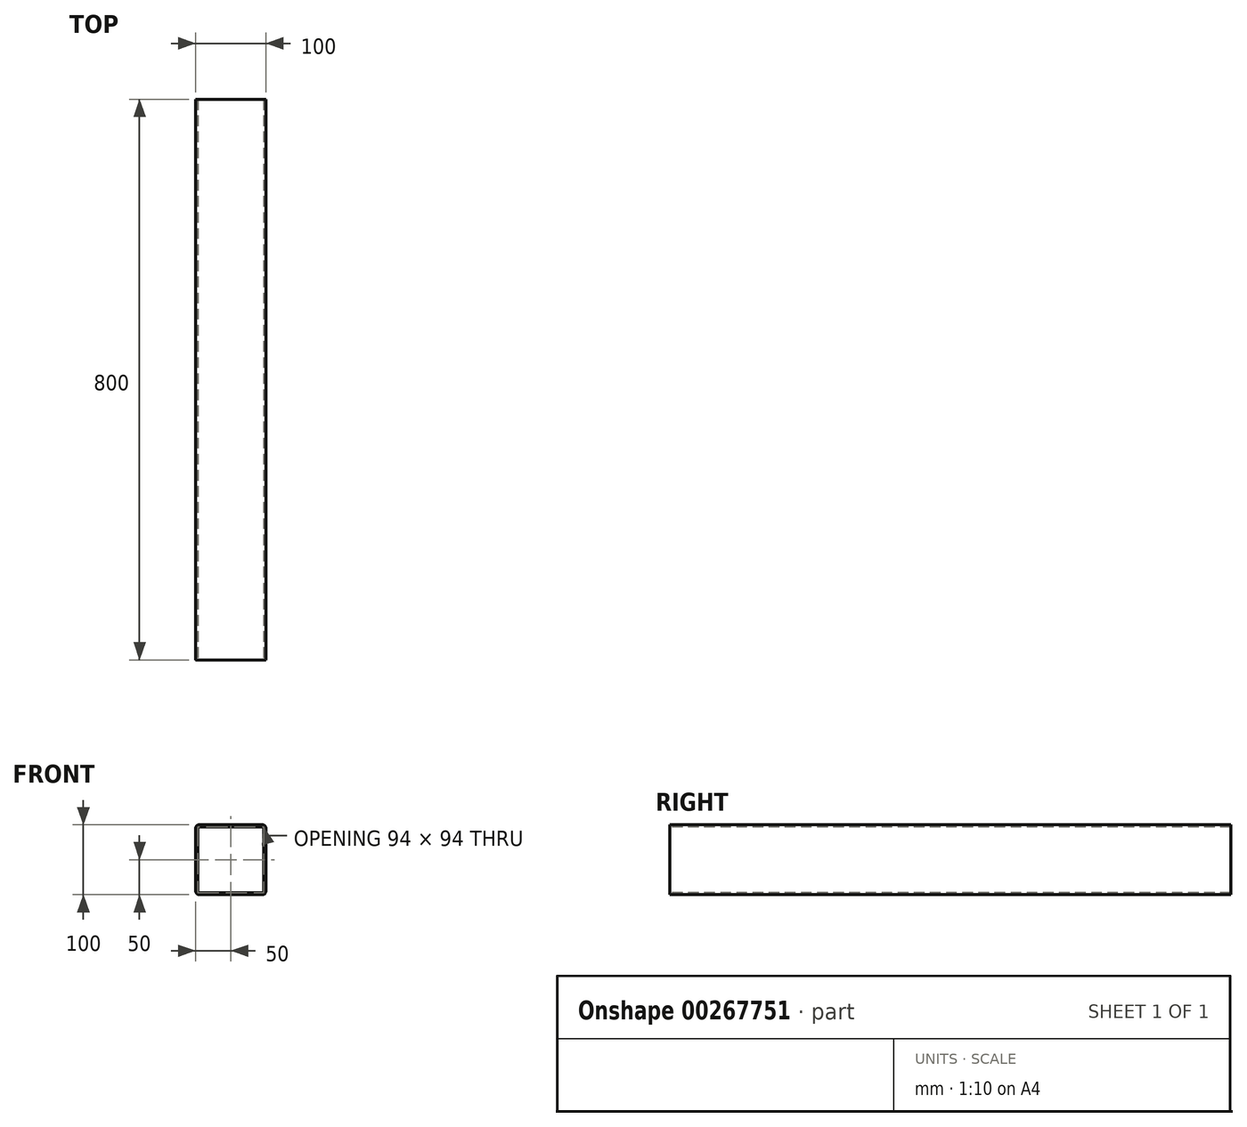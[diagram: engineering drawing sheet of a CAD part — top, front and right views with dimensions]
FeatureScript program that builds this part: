
annotation { "Feature Type Name" : "Feature", "Feature Type Description" : "" }
export const myFeature = defineFeature(function(context is Context, id is Id, definition is map)
    precondition{}
    {
        {
            var Q0;
            Q0=qCreatedBy(makeId("Front.planeOp"),FACE);
            var sketch = newSketch(context, id + "F0", { "sketchPlane" : qUnion([Q0])});
            skLineSegment(sketch, "E0.bottom", {"start": v(45, 50) * mm, "end": v(-45, 50) * mm});
            skLineSegment(sketch, "E0.top", {"start": v(45, -50) * mm, "end": v(-45, -50) * mm});
            skLineSegment(sketch, "E0.left", {"start": v(50, 45) * mm, "end": v(50, -45) * mm});
            skLineSegment(sketch, "E0.right", {"start": v(-50, 45) * mm, "end": v(-50, -45) * mm});
            skPoint(sketch, "E0.middle", {"position": v(0, 0) * mm});
            skPoint(sketch, "E1.visualSharp", {"position": v(-50, 50) * mm});
            skArc(sketch, "E1.filletArc", {"start": v(-45, 50) * mm, "mid": v(-48.54, 48.54) * mm, "end": v(-50, 45) * mm});
            skPoint(sketch, "E2.visualSharp", {"position": v(50, 50) * mm});
            skArc(sketch, "E2.filletArc", {"start": v(50, 45) * mm, "mid": v(48.54, 48.54) * mm, "end": v(45, 50) * mm});
            skPoint(sketch, "E3.visualSharp", {"position": v(50, -50) * mm});
            skArc(sketch, "E3.filletArc", {"start": v(45, -50) * mm, "mid": v(48.54, -48.54) * mm, "end": v(50, -45) * mm});
            skPoint(sketch, "E4.visualSharp", {"position": v(-50, -50) * mm});
            skArc(sketch, "E4.filletArc", {"start": v(-50, -45) * mm, "mid": v(-48.54, -48.54) * mm, "end": v(-45, -50) * mm});
            skArc(sketch, "E5.0", {"start": v(-45, 47) * mm, "mid": v(-46.41, 46.41) * mm, "end": v(-47, 45) * mm});
            skLineSegment(sketch, "E5.1", {"start": v(45, 47) * mm, "end": v(-45, 47) * mm});
            skLineSegment(sketch, "E5.2", {"start": v(-47, 45) * mm, "end": v(-47, -45) * mm});
            skArc(sketch, "E5.3", {"start": v(47, 45) * mm, "mid": v(46.41, 46.41) * mm, "end": v(45, 47) * mm});
            skArc(sketch, "E5.4", {"start": v(-47, -45) * mm, "mid": v(-46.41, -46.41) * mm, "end": v(-45, -47) * mm});
            skLineSegment(sketch, "E5.5", {"start": v(45, -47) * mm, "end": v(-45, -47) * mm});
            skArc(sketch, "E5.6", {"start": v(45, -47) * mm, "mid": v(46.41, -46.41) * mm, "end": v(47, -45) * mm});
            skLineSegment(sketch, "E5.7", {"start": v(47, 45) * mm, "end": v(47, -45) * mm});
            skSolve(sketch);
        }
        {
            var Q0;
            Q0=makeQuery(id+"F0.imprint","IMPRINT",FACE,{"disambiguationData":[TD([[makeQuery(id+"F0.imprint","IMPRINT",EDGE,{"derivedFrom":sQuery(id+"F0.wireOp",EDGE,"E0.bottom")}),1.0]])]});
            extrude(context, id + "F1", {"entities" : qUnion([Q0]), "oppositeDirection" : true, "depth" : 800 * mm});
        }
    });
